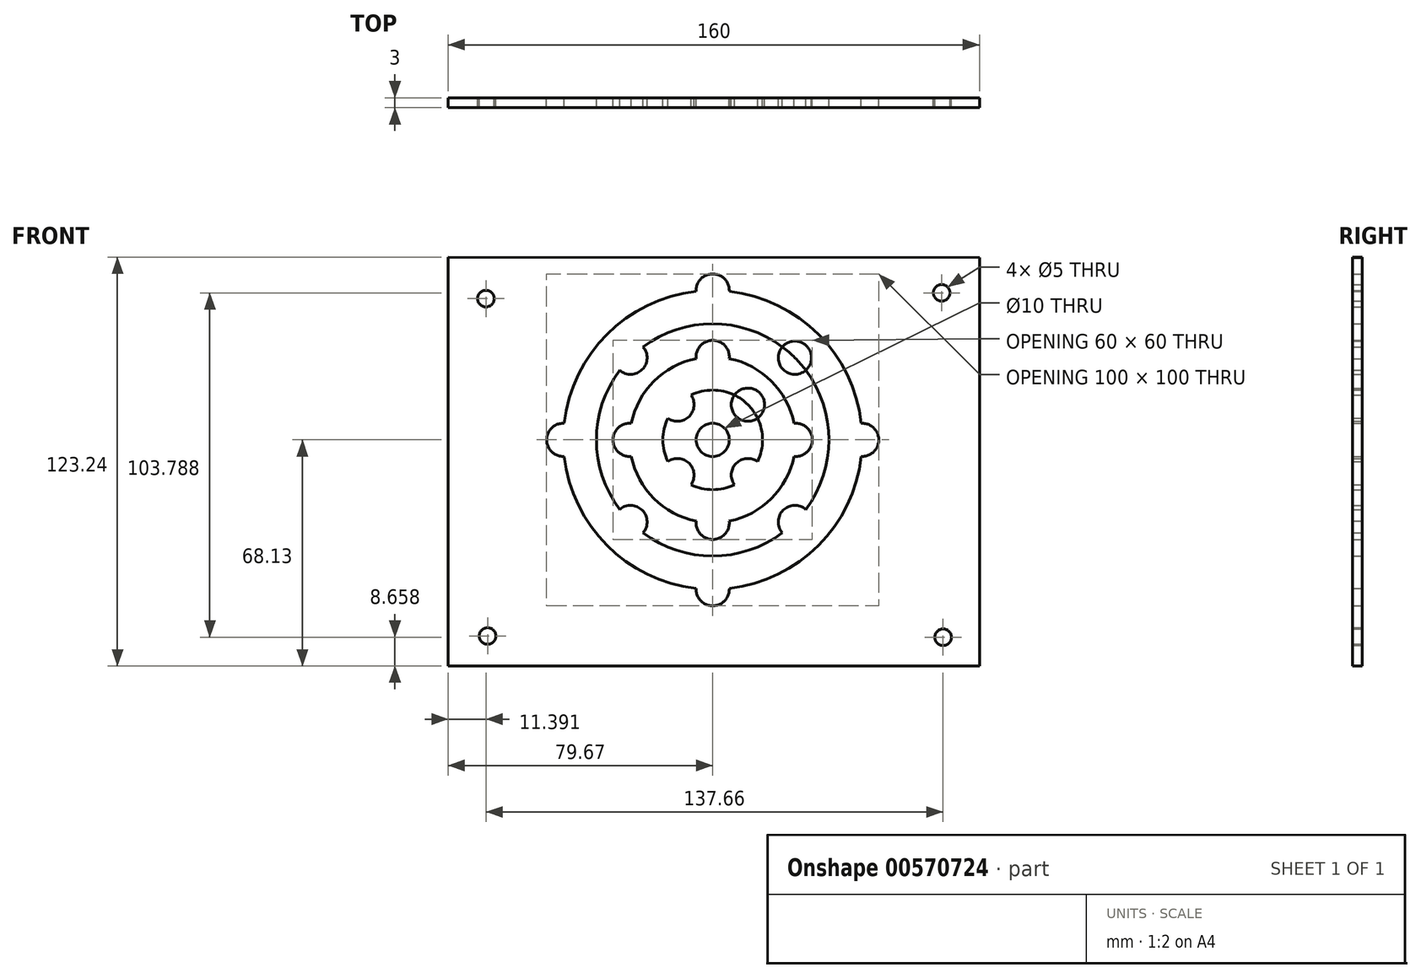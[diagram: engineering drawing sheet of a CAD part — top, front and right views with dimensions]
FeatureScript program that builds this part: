
annotation { "Feature Type Name" : "Feature", "Feature Type Description" : "" }
export const myFeature = defineFeature(function(context is Context, id is Id, definition is map)
    precondition{}
    {
        {
            var Q0;
            Q0=qCreatedBy(makeId("Front.planeOp"),FACE);
            var sketch = newSketch(context, id + "F0", { "sketchPlane" : qUnion([Q0])});
            skLineSegment(sketch, "E0.left", {"start": v(80, -68) * mm, "end": v(80, 55) * mm});
            skCircle(sketch, "E1", {"center": v(-68.6, 42.7) * mm, "radius": 2.5 * mm});
            skCircle(sketch, "E2", {"center": v(68.6, 44.45) * mm, "radius": 2.5 * mm});
            skCircle(sketch, "E3", {"center": v(69.05, -59.34) * mm, "radius": 2.5 * mm});
            skCircle(sketch, "E4", {"center": v(-68.1, -58.97) * mm, "radius": 2.5 * mm});
            skPoint(sketch, "E5", {"position": v(0, -86.06) * mm});
            skLineSegment(sketch, "E6", {"start": v(0, -68) * mm, "end": v(-80, -68) * mm});
            skLineSegment(sketch, "E7", {"start": v(-80, -68) * mm, "end": v(-80, 55.24) * mm});
            skLineSegment(sketch, "E8", {"start": v(-80, 55.24) * mm, "end": v(80, 55) * mm});
            skLineSegment(sketch, "E9", {"start": v(0, -68) * mm, "end": v(80, -68) * mm});
            skPoint(sketch, "E10.middle", {"position": v(-0.33, 0.13) * mm});
            skLineSegment(sketch, "E11.bottom", {"start": v(49.67, -49.87) * mm, "end": v(-50.33, -49.87) * mm});
            skLineSegment(sketch, "E11.top", {"start": v(49.67, 50.13) * mm, "end": v(-50.33, 50.13) * mm});
            skLineSegment(sketch, "E11.left", {"start": v(49.67, -49.87) * mm, "end": v(49.67, 50.13) * mm});
            skLineSegment(sketch, "E11.right", {"start": v(-50.33, -49.87) * mm, "end": v(-50.33, 50.13) * mm});
            skCircle(sketch, "E12", {"center": v(-0.33, 0.13) * mm, "radius": 15 * mm});
            skCircle(sketch, "E13", {"center": v(-0.33, 0.13) * mm, "radius": 25 * mm});
            skCircle(sketch, "E14", {"center": v(-0.33, 0.13) * mm, "radius": 35 * mm});
            skCircle(sketch, "E15", {"center": v(-0.33, 0.13) * mm, "radius": 45 * mm});
            skCircle(sketch, "E16", {"center": v(-0.33, 0.13) * mm, "radius": 5 * mm});
            skCircle(sketch, "E17", {"center": v(-25.33, 0.13) * mm, "radius": 5 * mm});
            skCircle(sketch, "E18", {"center": v(44.67, 0.13) * mm, "radius": 5 * mm});
            skCircle(sketch, "E19", {"center": v(24.67, 0.13) * mm, "radius": 5 * mm});
            skCircle(sketch, "E20", {"center": v(-0.33, 45.13) * mm, "radius": 5 * mm});
            skCircle(sketch, "E21", {"center": v(-0.33, -44.87) * mm, "radius": 5 * mm});
            skCircle(sketch, "E22", {"center": v(-0.33, -24.87) * mm, "radius": 5 * mm});
            skCircle(sketch, "E23", {"center": v(-0.33, 25.13) * mm, "radius": 5 * mm});
            skCircle(sketch, "E24", {"center": v(-25.08, -24.62) * mm, "radius": 5 * mm});
            skCircle(sketch, "E25", {"center": v(-10.94, -10.48) * mm, "radius": 5 * mm});
            skCircle(sketch, "E26", {"center": v(10.28, 10.74) * mm, "radius": 5 * mm});
            skCircle(sketch, "E27", {"center": v(24.42, 24.88) * mm, "radius": 5 * mm});
            skCircle(sketch, "E28", {"center": v(-25.08, 24.88) * mm, "radius": 5 * mm});
            skCircle(sketch, "E29", {"center": v(-10.94, 10.74) * mm, "radius": 5 * mm});
            skCircle(sketch, "E30", {"center": v(10.28, -10.48) * mm, "radius": 5 * mm});
            skCircle(sketch, "E31", {"center": v(-45.33, 0.13) * mm, "radius": 5 * mm});
            skCircle(sketch, "E32", {"center": v(24.42, -24.62) * mm, "radius": 5 * mm});
            skSolve(sketch);
        }
        {
            var Q0;
            Q0=makeQuery(id+"F0.imprint","IMPRINT",FACE,{"disambiguationData":[TD([[makeQuery(id+"F0.imprint","IMPRINT",EDGE,{"derivedFrom":sQuery(id+"F0.wireOp",EDGE,"E0.left")}),1.0]])]});
            var Q1;
            {var subQ5=sQuery(id+"F0.wireOp",EDGE,"E11.right");var subQ6=sQuery(id+"F0.wireOp",EDGE,"E11.top");var subQ7=makeQuery(id+"F0.imprint","INTERSECT",VERTEX,{"derivedFrom":[subQ6,subQ5]});Q1=makeQuery(id+"F0.imprint","IMPRINT",FACE,{"disambiguationData":[TD([[makeQuery(id+"F0.imprint","IMPRINT",EDGE,{"disambiguationData":[TD([[subQ7,1.0]])],"derivedFrom":subQ6}),1.0]])]});}
            var Q2;
            {var subQ1=sQuery(id+"F0.wireOp",EDGE,"E11.bottom");var subQ7=sQuery(id+"F0.wireOp",EDGE,"E11.right");var subQ8=makeQuery(id+"F0.imprint","INTERSECT",VERTEX,{"derivedFrom":[subQ1,subQ7]});Q2=makeQuery(id+"F0.imprint","IMPRINT",FACE,{"disambiguationData":[TD([[makeQuery(id+"F0.imprint","IMPRINT",EDGE,{"disambiguationData":[TD([[subQ8,1.0]])],"derivedFrom":subQ1}),-1.0]])]});}
            var Q3;
            {var subQ5=sQuery(id+"F0.wireOp",EDGE,"E11.left");var subQ6=sQuery(id+"F0.wireOp",EDGE,"E11.bottom");var subQ7=makeQuery(id+"F0.imprint","INTERSECT",VERTEX,{"derivedFrom":[subQ6,subQ5]});Q3=makeQuery(id+"F0.imprint","IMPRINT",FACE,{"disambiguationData":[TD([[makeQuery(id+"F0.imprint","IMPRINT",EDGE,{"disambiguationData":[TD([[subQ7,-1.0]])],"derivedFrom":subQ6}),-1.0]])]});}
            var Q4;
            {var subQ1=sQuery(id+"F0.wireOp",EDGE,"E11.left");var subQ7=sQuery(id+"F0.wireOp",EDGE,"E11.top");var subQ8=makeQuery(id+"F0.imprint","INTERSECT",VERTEX,{"derivedFrom":[subQ7,subQ1]});Q4=makeQuery(id+"F0.imprint","IMPRINT",FACE,{"disambiguationData":[TD([[makeQuery(id+"F0.imprint","IMPRINT",EDGE,{"disambiguationData":[TD([[subQ8,-1.0]])],"derivedFrom":subQ7}),1.0]])]});}
            var Q5;
            {var subQ12=sQuery(id+"F0.wireOp",EDGE,"E27");var subQ13=sQuery(id+"F0.wireOp",EDGE,"E14");var subQ14=makeQuery(id+"F0.imprint","INTERSECT",VERTEX,{"disambiguationData":[OD(0.0)],"derivedFrom":[subQ13,subQ12]});Q5=makeQuery(id+"F0.imprint","IMPRINT",FACE,{"disambiguationData":[TD([[makeQuery(id+"F0.imprint","IMPRINT",EDGE,{"disambiguationData":[TD([[subQ14,-1.0]])],"derivedFrom":subQ13}),-1.0]])]});}
            var Q6;
            {var subQ1=sQuery(id+"F0.wireOp",EDGE,"E13");var subQ4=sQuery(id+"F0.wireOp",EDGE,"E23");var subQ18=makeQuery(id+"F0.imprint","INTERSECT",VERTEX,{"disambiguationData":[OD(0.0)],"derivedFrom":[subQ1,subQ4]});Q6=makeQuery(id+"F0.imprint","IMPRINT",FACE,{"disambiguationData":[TD([[makeQuery(id+"F0.imprint","IMPRINT",EDGE,{"disambiguationData":[TD([[subQ18,1.0]])],"derivedFrom":subQ1}),-1.0]])]});}
            var Q7;
            {var subQ11=sQuery(id+"F0.wireOp",EDGE,"E26");var subQ12=sQuery(id+"F0.wireOp",EDGE,"E12");var subQ13=makeQuery(id+"F0.imprint","INTERSECT",VERTEX,{"disambiguationData":[OD(0.0)],"derivedFrom":[subQ12,subQ11]});Q7=makeQuery(id+"F0.imprint","IMPRINT",FACE,{"disambiguationData":[TD([[makeQuery(id+"F0.imprint","IMPRINT",EDGE,{"disambiguationData":[TD([[subQ13,-1.0]])],"derivedFrom":subQ12}),-1.0]])]});}
            var Q8;
            Q8=makeQuery(id+"F0.imprint","IMPRINT",FACE,{"disambiguationData":[TD([[makeQuery(id+"F0.imprint","IMPRINT",EDGE,{"derivedFrom":sQuery(id+"F0.wireOp",EDGE,"E16")}),-1.0]])]});
            extrude(context, id + "F1", {"entities" : qUnion([Q0, Q1, Q2, Q3, Q4, Q5, Q6, Q7, Q8]), "depth" : 3 * mm, "offsetDistance" : 25 * mm});
        }
    });
